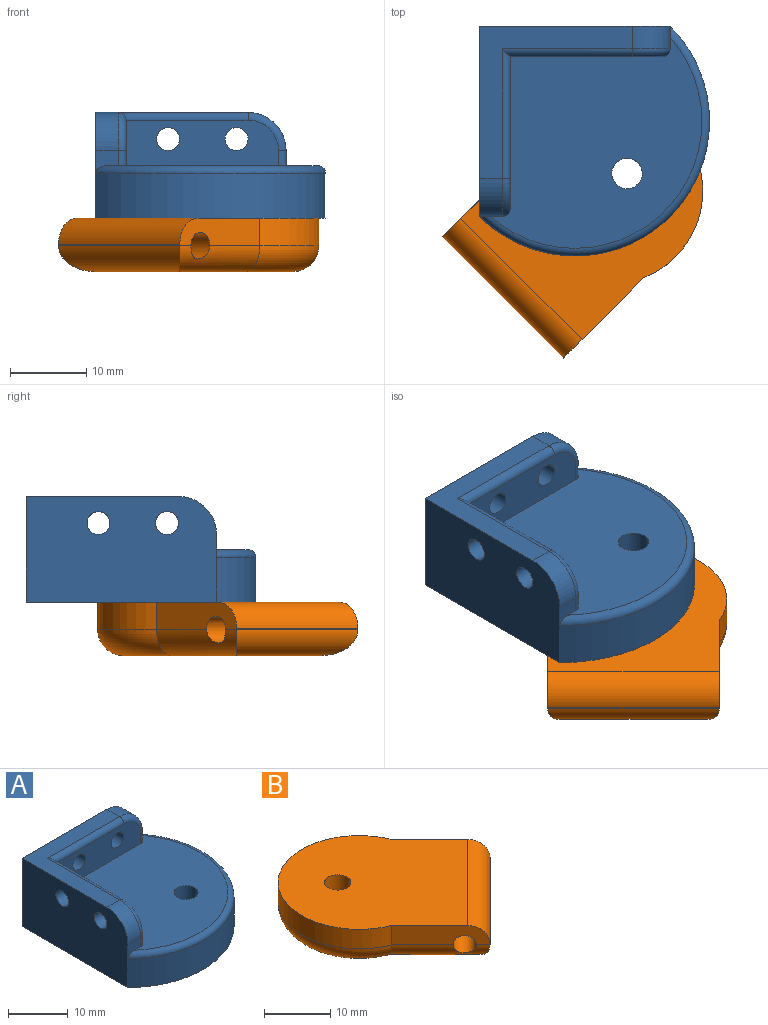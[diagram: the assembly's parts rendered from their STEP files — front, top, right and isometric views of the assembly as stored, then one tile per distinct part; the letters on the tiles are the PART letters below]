
ASSEMBLY  parts=2 mates=1
PART A: 24 faces, bbox 32.7x32.7x14.3 mm
  f0: plane 27.72x27.72mm, normal (0,0,1), area 554.3mm2, adj f4,f6,f7,f8,f9,f13,f18,f23
  f1: plane 25x13.9mm, normal (0,1,0), area 328mm2, adj f2,f3,f5,f6,f10,f12,f21,f22
  f2: plane 25x13.9mm, normal (-1,0,0), area 328mm2, adj f1,f3,f5,f7,f10,f11,f19,f20
  f3: cylinder r=17.68mm len=30.18mm, axis (0,0,1), area 327.7mm2, adj f1,f2,f5,f23
  f4: cylinder r=2mm len=6.9mm, axis (0,0,1), area 86.7mm2, adj f0,f5
  f5: plane 30.18x30.18mm, normal (0,0,-1), area 790.8mm2, adj f1,f2,f3,f4
  f6: plane 3x3mm, normal (1,0,0), area 6.3mm2, adj f0,f1,f12,f18,f23
  f7: plane 3x3mm, normal (0,-1,0), area 6.3mm2, adj f0,f2,f11,f13,f23
  f8: plane 20x6mm, normal (1,0,0), area 102.4mm2, adj f0,f9,f13,f14,f15,f19,f20
  f9: plane 20x6mm, normal (0,-1,0), area 102.4mm2, adj f0,f8,f16,f17,f18,f21,f22
  f10: plane 20x20mm, normal (0,0,1), area 111mm2, adj f1,f2,f11,f12,f15,f16
  f11: cylinder r=5mm len=5mm, axis (-1,0,0), area 23.6mm2, adj f2,f7,f10,f14
  f12: cylinder r=5mm len=5mm, axis (0,-1,0), area 23.6mm2, adj f1,f6,f10,f17
  f13: cylinder r=1mm len=2mm, axis (0,0,1), area 3.1mm2, adj f0,f7,f8,f14
  f14: torus R=4mm, axis (1,0,0), area 11.4mm2, adj f8,f11,f13,f15
  f15: cylinder r=1mm len=17mm, axis (0,-1,0), area 25.7mm2, adj f8,f10,f14,f16
  f16: cylinder r=1mm len=17mm, axis (-1,0,0), area 25.7mm2, adj f9,f10,f15,f17
  f17: torus R=4mm, axis (0,1,0), area 11.4mm2, adj f9,f12,f16,f18
  f18: cylinder r=1mm len=2mm, axis (0,0,1), area 3.1mm2, adj f0,f6,f9,f17
  f19: cylinder r=1.5mm len=4mm, axis (1,0,0), area 37.7mm2, adj f2,f8
  f20: cylinder r=1.5mm len=4mm, axis (1,0,0), area 37.7mm2, adj f2,f8
  f21: cylinder r=1.5mm len=4mm, axis (0,-1,0), area 37.7mm2, adj f1,f9
  f22: cylinder r=1.5mm len=4mm, axis (0,-1,0), area 37.7mm2, adj f1,f9
  f23: torus R=16.68mm, axis (0,0,1), area 84.3mm2, adj f0,f3,f6,f7
PART B: 13 faces, bbox 35.2x35.2x7 mm
  f0: plane 10.52x10.52mm, normal (-0.71,-0.71,0), area 46.3mm2, adj f1,f4,f6,f7,f8,f12
  f1: cylinder r=12.26mm len=23.66mm, axis (0,0,1), area 174.7mm2, adj f0,f2,f6,f9
  f2: plane 10.52x10.52mm, normal (0.71,0.71,0), area 46.3mm2, adj f1,f4,f6,f7,f11,f12
  f3: cylinder r=2mm len=7mm, axis (0,0,1), area 88mm2, adj f5,f6
  f4: plane 15.91x15.91mm, normal (0.71,-0.71,0), area 4.5mm2, adj f0,f2,f7,f10
  f5: plane 25.96x25.96mm, normal (0,0,-1), area 372.8mm2, adj f3,f8,f9,f10,f11
  f6: plane 31.77x31.77mm, normal (0,0,1), area 597.8mm2, adj f0,f1,f2,f3,f7
  f7: cylinder r=3.4mm len=18.31mm, axis (-0.71,-0.71,0), area 120.2mm2, adj f0,f2,f4,f6
  f8: cylinder r=3.4mm len=13.46mm, axis (0.71,-0.71,0), area 69.3mm2, adj f0,f5,f9,f10,f12
  f9: torus R=8.86mm, axis (0,0,-1), area 235.6mm2, adj f1,f5,f8,f11
  f10: cylinder r=3.4mm len=18.31mm, axis (0.71,0.71,0), area 107mm2, adj f4,f5,f8,f11
  f11: cylinder r=3.4mm len=13.46mm, axis (-0.71,0.71,0), area 69.3mm2, adj f2,f5,f9,f10,f12
  f12: cylinder r=1.75mm len=18.38mm, axis (-0.71,-0.71,0), area 244.8mm2, adj f0,f2,f8,f11
PLACE A at identity
PLACE B rot(axis=(0,0,-1),90deg) t=(19.04,-10.24,25)mm
MATE revolute B.f3 <-> A.f4  axis (0,0,1) through (1.3,-17.73,-6.9)mm
